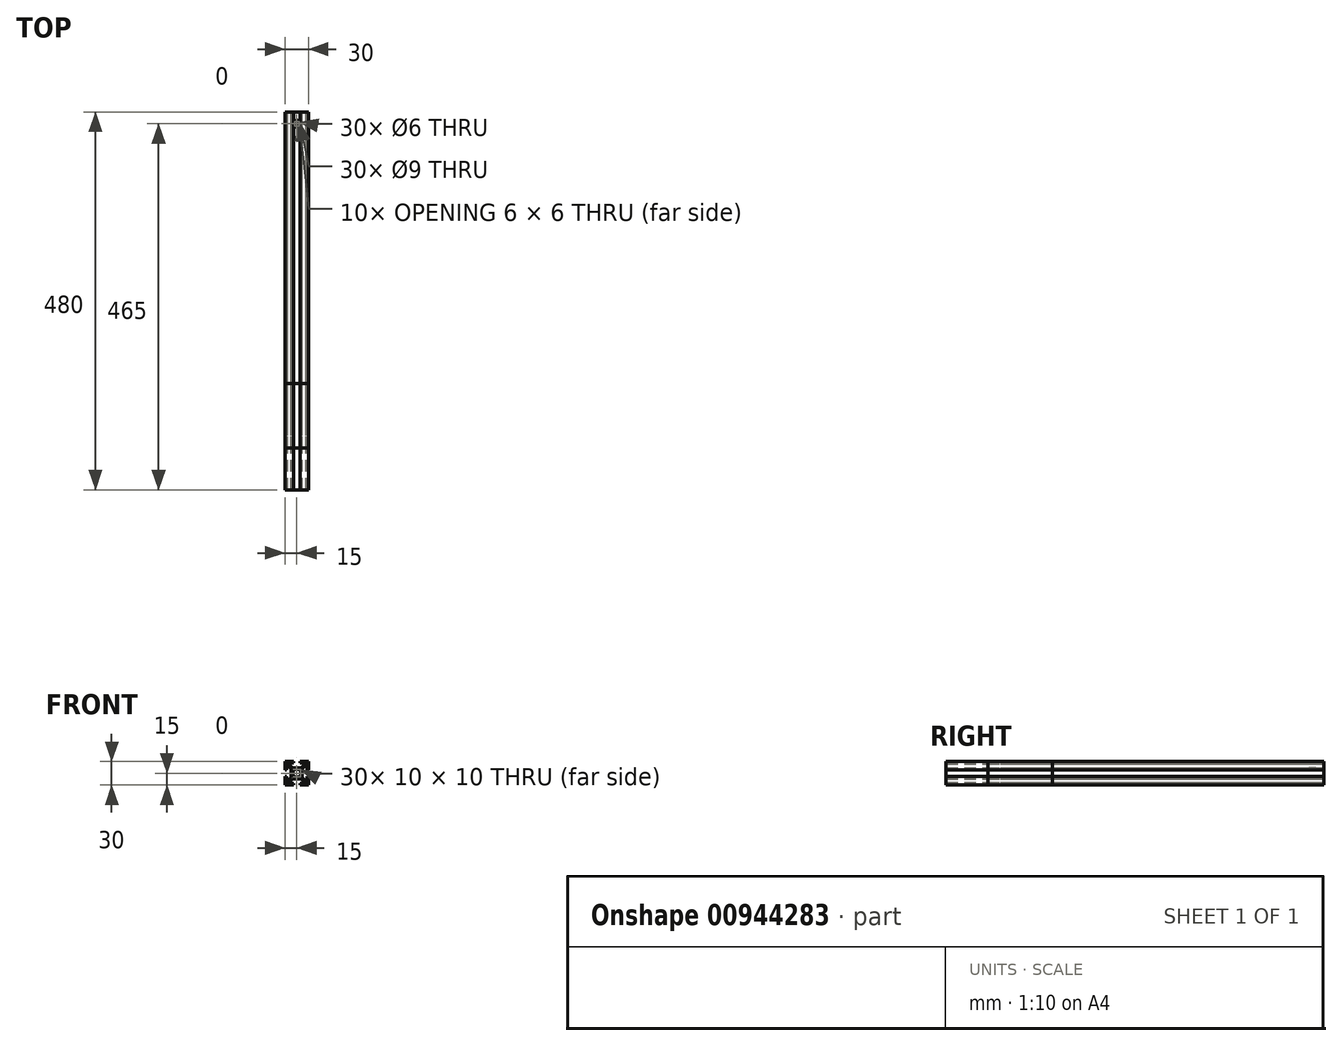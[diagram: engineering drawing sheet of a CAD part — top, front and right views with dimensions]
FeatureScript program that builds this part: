
annotation { "Feature Type Name" : "Feature", "Feature Type Description" : "" }
export const myFeature = defineFeature(function(context is Context, id is Id, definition is map)
    precondition{}
    {
        {
            var Q0;
            Q0=qCreatedBy(makeId("Front.planeOp"),FACE);
            var sketch = newSketch(context, id + "F0", { "sketchPlane" : qUnion([Q0])});
            skLineSegment(sketch, "E0.bottom", {"start": v(5, -5) * mm, "end": v(-5, -5) * mm});
            skLineSegment(sketch, "E0.top", {"start": v(5, 5) * mm, "end": v(-5, 5) * mm});
            skLineSegment(sketch, "E0.left", {"start": v(5, -5) * mm, "end": v(5, 5) * mm});
            skLineSegment(sketch, "E0.right", {"start": v(-5, -5) * mm, "end": v(-5, 5) * mm});
            skPoint(sketch, "E0.middle", {"position": v(0, 0) * mm});
            skLineSegment(sketch, "E1.bottom", {"start": v(-15, 15) * mm, "end": v(-4, 15) * mm});
            skLineSegment(sketch, "E1.top", {"start": v(-15, -15) * mm, "end": v(-4, -15) * mm});
            skLineSegment(sketch, "E1.left", {"start": v(-15, 15) * mm, "end": v(-15, 4) * mm});
            skLineSegment(sketch, "E1.right", {"start": v(15, 15) * mm, "end": v(15, 4) * mm});
            skLineSegment(sketch, "E2", {"start": v(-15, 4) * mm, "end": v(-13, 4) * mm});
            skLineSegment(sketch, "E3", {"start": v(-13, 4) * mm, "end": v(-13, 11.5) * mm});
            skLineSegment(sketch, "E4", {"start": v(-13, 11.5) * mm, "end": v(-7, 5.5) * mm});
            skLineSegment(sketch, "E5", {"start": v(-7, 5.5) * mm, "end": v(-7, -5.5) * mm});
            skLineSegment(sketch, "E6", {"start": v(-7, -5.5) * mm, "end": v(-13, -11.5) * mm});
            skLineSegment(sketch, "E7", {"start": v(-13, -11.5) * mm, "end": v(-13, -4) * mm});
            skLineSegment(sketch, "E8", {"start": v(-13, -4) * mm, "end": v(-15, -4) * mm});
            skLineSegment(sketch, "E9", {"start": v(-30.6, 0) * mm, "end": v(36.58, 0) * mm, "construction": true});
            skLineSegment(sketch, "E10", {"start": v(0, -25.45) * mm, "end": v(0, 23.58) * mm, "construction": true});
            skLineSegment(sketch, "E11.1.0", {"start": v(-4, -15) * mm, "end": v(-4, -13) * mm});
            skLineSegment(sketch, "E11.1.1", {"start": v(-4, -13) * mm, "end": v(-11.5, -13) * mm});
            skLineSegment(sketch, "E11.1.2", {"start": v(-11.5, -13) * mm, "end": v(-5.5, -7) * mm});
            skLineSegment(sketch, "E11.1.3", {"start": v(-5.5, -7) * mm, "end": v(5.5, -7) * mm});
            skLineSegment(sketch, "E11.1.4", {"start": v(5.5, -7) * mm, "end": v(11.5, -13) * mm});
            skLineSegment(sketch, "E11.1.5", {"start": v(11.5, -13) * mm, "end": v(4, -13) * mm});
            skLineSegment(sketch, "E11.1.6", {"start": v(4, -13) * mm, "end": v(4, -15) * mm});
            skLineSegment(sketch, "E11.2.0", {"start": v(15, -4) * mm, "end": v(13, -4) * mm});
            skLineSegment(sketch, "E11.2.1", {"start": v(13, -4) * mm, "end": v(13, -11.5) * mm});
            skLineSegment(sketch, "E11.2.2", {"start": v(13, -11.5) * mm, "end": v(7, -5.5) * mm});
            skLineSegment(sketch, "E11.2.3", {"start": v(7, -5.5) * mm, "end": v(7, 5.5) * mm});
            skLineSegment(sketch, "E11.2.4", {"start": v(7, 5.5) * mm, "end": v(13, 11.5) * mm});
            skLineSegment(sketch, "E11.2.5", {"start": v(13, 11.5) * mm, "end": v(13, 4) * mm});
            skLineSegment(sketch, "E11.2.6", {"start": v(13, 4) * mm, "end": v(15, 4) * mm});
            skLineSegment(sketch, "E11.3.0", {"start": v(4, 15) * mm, "end": v(4, 13) * mm});
            skLineSegment(sketch, "E11.3.1", {"start": v(4, 13) * mm, "end": v(11.5, 13) * mm});
            skLineSegment(sketch, "E11.3.2", {"start": v(11.5, 13) * mm, "end": v(5.5, 7) * mm});
            skLineSegment(sketch, "E11.3.3", {"start": v(5.5, 7) * mm, "end": v(-5.5, 7) * mm});
            skLineSegment(sketch, "E11.3.4", {"start": v(-5.5, 7) * mm, "end": v(-11.5, 13) * mm});
            skLineSegment(sketch, "E11.3.5", {"start": v(-11.5, 13) * mm, "end": v(-4, 13) * mm});
            skLineSegment(sketch, "E11.3.6", {"start": v(-4, 13) * mm, "end": v(-4, 15) * mm});
            skLineSegment(sketch, "E12.trimOffspring", {"start": v(4, -15) * mm, "end": v(15, -15) * mm});
            skLineSegment(sketch, "E13.trimOffspring", {"start": v(15, -4) * mm, "end": v(15, -15) * mm});
            skLineSegment(sketch, "E14.trimOffspring", {"start": v(4, 15) * mm, "end": v(15, 15) * mm});
            skLineSegment(sketch, "E15.trimOffspring", {"start": v(-15, -4) * mm, "end": v(-15, -15) * mm});
            skSolve(sketch);
        }
        {
            var Q0;
            Q0=makeQuery(id+"F0.imprint","IMPRINT",FACE,{"disambiguationData":[TD([[makeQuery(id+"F0.imprint","IMPRINT",EDGE,{"derivedFrom":sQuery(id+"F0.wireOp",EDGE,"E0.bottom")}),1.0]])]});
            extrude(context, id + "F1", {"entities" : qUnion([Q0]), "depth" : 480 * mm, "offsetDistance" : 25 * mm});
        }
        {
            var Q0;
            Q0=qSketchRegion(id+"F0",true);
            extrude(context, id + "F2", {"entities" : qUnion([Q0]), "depth" : 427 * mm, "offsetDistance" : 25 * mm});
        }
        {
            var Q0;
            Q0=qSketchRegion(id+"F0",true);
            extrude(context, id + "F3", {"entities" : qUnion([Q0]), "depth" : 345 * mm, "offsetDistance" : 25 * mm});
        }
        {
            var Q0;
            Q0=makeQuery(id+"F1.opExtrude","SWEPT_FACE",FACE,{"disambiguationData":[OSD([sQuery(id+"F0.wireOp",EDGE,"E11.3.3")])]});
            var sketch = newSketch(context, id + "F4", { "sketchPlane" : qUnion([Q0])});
            skLineSegment(sketch, "E16", {"start": v(0, 0) * mm, "end": v(0, -35.29) * mm, "construction": true});
            skCircle(sketch, "E17", {"center": v(0, -15) * mm, "radius": 3 * mm});
            skSolve(sketch);
        }
        {
            var Q0;
            Q0=makeQuery(id+"F4.imprint","IMPRINT",FACE,{"disambiguationData":[TD([[makeQuery(id+"F4.imprint","IMPRINT",EDGE,{"derivedFrom":sQuery(id+"F4.wireOp",EDGE,"E17")}),1.0]])]});
            extrude(context, id + "F5", {"entities" : qUnion([Q0]), "operationType" : NewBodyOperationType.REMOVE, "endBound" : BoundingType.THROUGH_ALL, "oppositeDirection" : true, "depth" : 3 * mm, "offsetDistance" : 25 * mm});
        }
        {
            var Q0;
            Q0=makeQuery(id+"F1.opExtrude","SWEPT_FACE",FACE,{"disambiguationData":[OSD([sQuery(id+"F0.wireOp",EDGE,"E11.3.3")])]});
            var sketch = newSketch(context, id + "F6", { "sketchPlane" : qUnion([Q0])});
            skCircle(sketch, "E18", {"center": v(0, -15) * mm, "radius": 4.5 * mm});
            skSolve(sketch);
        }
        {
            var Q0;
            Q0=makeQuery(id+"F6.imprint","IMPRINT",FACE,{"disambiguationData":[TD([[makeQuery(id+"F6.imprint","IMPRINT",EDGE,{"derivedFrom":sQuery(id+"F6.wireOp",EDGE,"E18")}),1.0]])]});
            extrude(context, id + "F7", {"entities" : qUnion([Q0]), "operationType" : NewBodyOperationType.REMOVE, "depth" : 25 * mm, "offsetDistance" : 25 * mm, "hasSecondDirection" : true, "secondDirectionOppositeDirection" : true, "secondDirectionDepth" : 3 * mm});
        }
        {
            var Q0;
            Q0=makeQuery(id+"F5.boolean.opBoolean","INTERSECT",EDGE,{"derivedFrom":[makeQuery(id+"F1.opExtrude","SWEPT_FACE",FACE,{"disambiguationData":[OSD([sQuery(id+"F0.wireOp",EDGE,"E0.bottom")])]}),makeQuery(id+"F5.opExtrude","SWEPT_FACE",FACE,{"disambiguationData":[OSD([sQuery(id+"F4.wireOp",EDGE,"E17")])]})]});
            chamfer(context, id + "F8", {"entities" : qUnion([Q0]), "width" : 1 * mm, "tangentPropagation" : true});
        }
    });
